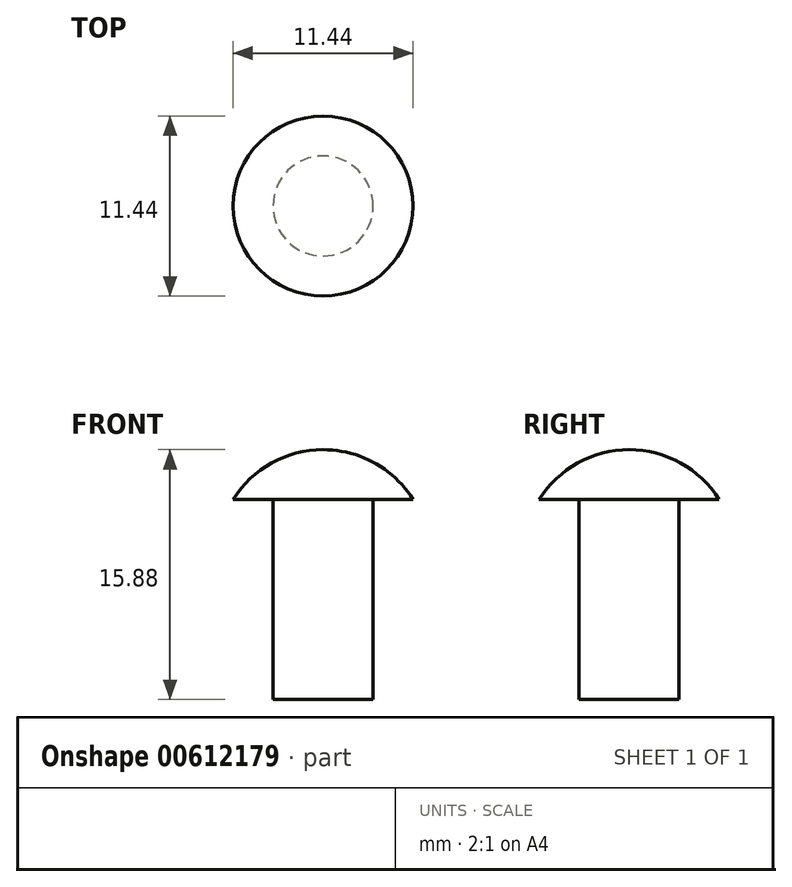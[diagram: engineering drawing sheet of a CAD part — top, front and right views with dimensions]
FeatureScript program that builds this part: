
annotation { "Feature Type Name" : "Feature", "Feature Type Description" : "" }
export const myFeature = defineFeature(function(context is Context, id is Id, definition is map)
    precondition{}
    {
        {
            var Q0;
            Q0=qCreatedBy(makeId("Front.planeOp"),FACE);
            var sketch = newSketch(context, id + "F0", { "sketchPlane" : qUnion([Q0])});
            skLineSegment(sketch, "E0", {"start": v(0, 0) * mm, "end": v(3.17, 0) * mm});
            skLineSegment(sketch, "E1", {"start": v(3.17, 0) * mm, "end": v(3.17, 12.7) * mm});
            skLineSegment(sketch, "E2", {"start": v(3.18, 12.7) * mm, "end": v(5.72, 12.7) * mm});
            skLineSegment(sketch, "E3", {"start": v(0, 0) * mm, "end": v(0, 15.88) * mm});
            skArc(sketch, "E4", {"start": v(5.72, 12.7) * mm, "mid": v(3.27, 15.03) * mm, "end": v(0, 15.88) * mm});
            skLineSegment(sketch, "E5", {"start": v(0, 0) * mm, "end": v(0, -16.17) * mm, "construction": true});
            skSolve(sketch);
        }
        {
            var Q0;
            Q0=makeQuery(id+"F0.imprint","IMPRINT",FACE,{"disambiguationData":[TD([[makeQuery(id+"F0.imprint","IMPRINT",EDGE,{"derivedFrom":sQuery(id+"F0.wireOp",EDGE,"E0")}),1.0]])]});
            var Q1;
            Q1=sQuery(id+"F0.wireOp",EDGE,"E5");
            revolve(context, id + "F1", {"entities" : qUnion([Q0]), "axis" : qUnion([Q1]), "revolveType" : RevolveType.FULL});
        }
    });
